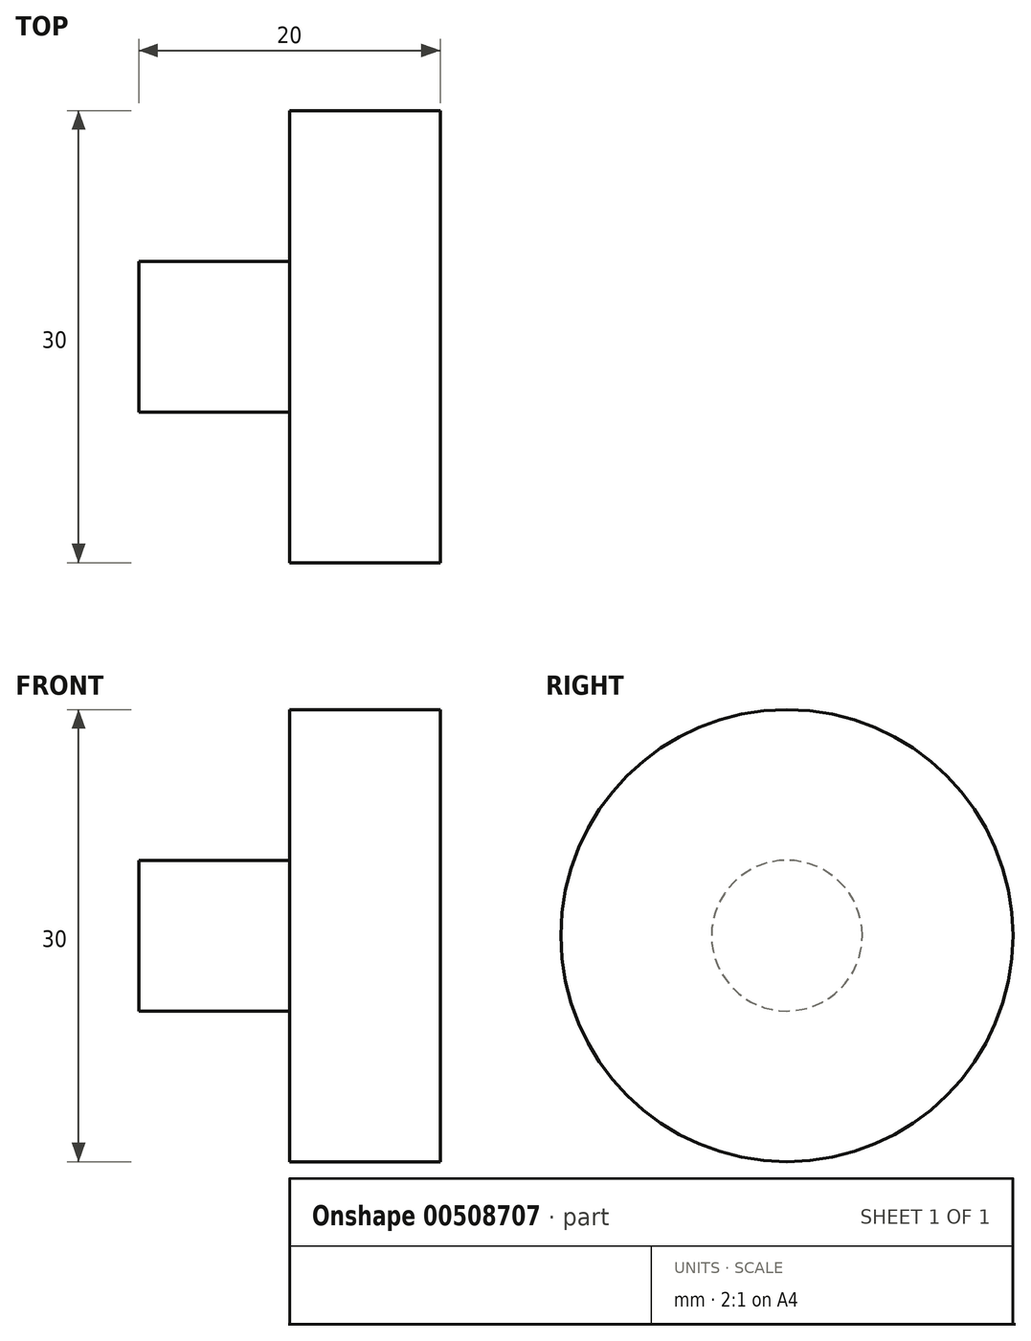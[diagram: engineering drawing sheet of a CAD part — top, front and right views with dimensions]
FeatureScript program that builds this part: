
annotation { "Feature Type Name" : "Feature", "Feature Type Description" : "" }
export const myFeature = defineFeature(function(context is Context, id is Id, definition is map)
    precondition{}
    {
        {
            var Q0;
            Q0=qCreatedBy(makeId("Front.planeOp"),FACE);
            var sketch = newSketch(context, id + "F0", { "sketchPlane" : qUnion([Q0])});
            skLineSegment(sketch, "E0.bottom", {"start": v(0, 5) * mm, "end": v(10, 5) * mm});
            skLineSegment(sketch, "E0.top", {"start": v(0, 0) * mm, "end": v(20, 0) * mm});
            skLineSegment(sketch, "E0.left", {"start": v(0, 5) * mm, "end": v(0, 0) * mm});
            skLineSegment(sketch, "E0.right", {"start": v(20, 5) * mm, "end": v(20, 0) * mm});
            skLineSegment(sketch, "E1.left", {"start": v(20, 5) * mm, "end": v(20, 15) * mm});
            skLineSegment(sketch, "E1.right", {"start": v(10, 5) * mm, "end": v(10, 15) * mm});
            skLineSegment(sketch, "E2", {"start": v(10, 15) * mm, "end": v(20, 15) * mm});
            skLineSegment(sketch, "E3", {"start": v(0, 66.32) * mm, "end": v(0, -57.72) * mm});
            skLineSegment(sketch, "E4", {"start": v(-60.71, 0) * mm, "end": v(74.91, 0) * mm, "construction": true});
            skSolve(sketch);
        }
        {
            var Q0;
            Q0 = qSketchRegion(id + "F0", true);
            var Q1;
            Q1=sQuery(id+"F0.wireOp",EDGE,"E4");
            revolve(context, id + "F1", {"surfaceOperationType" : NewSurfaceOperationType.NEW, "entities" : qUnion([Q0]), "axis" : qUnion([Q1]), "revolveType" : RevolveType.FULL});
        }
        {
            var Q0;
            Q0=qCreatedBy(makeId("Front.planeOp"),FACE);
            cPlane(context, id + "F2", {"entities" : qUnion([Q0]), "cplaneType" : CPlaneType.OFFSET, "offset" : 40 * mm, "width" : 150 * mm, "height" : 150 * mm});
        }
    });
